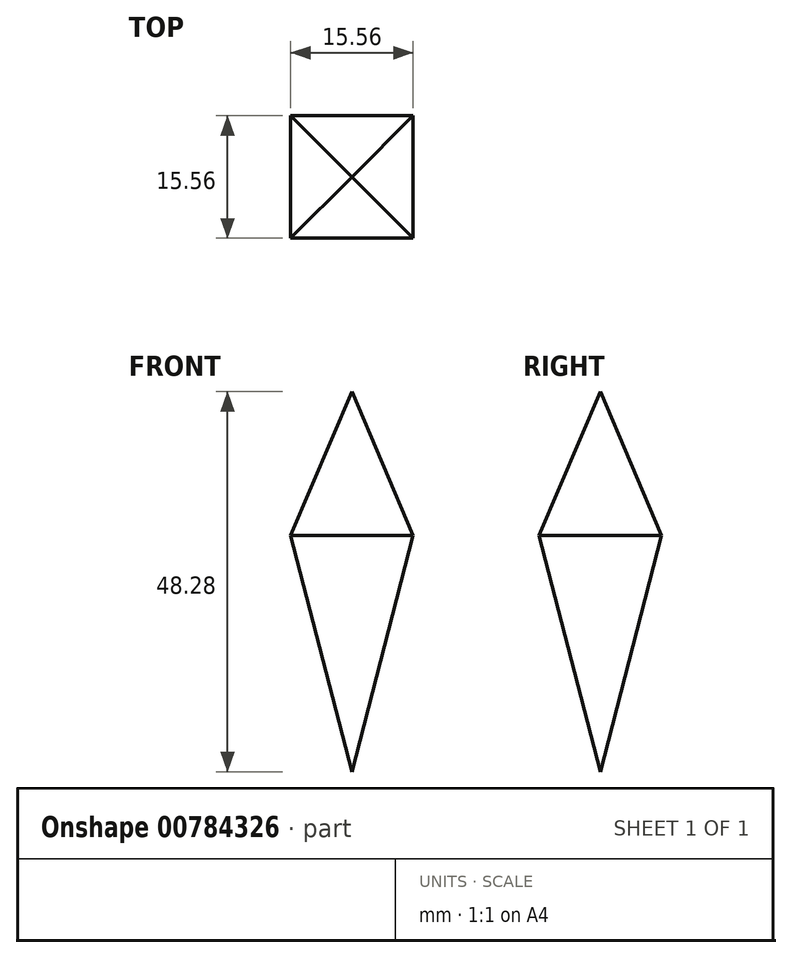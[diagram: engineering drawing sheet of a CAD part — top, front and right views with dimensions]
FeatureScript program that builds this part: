
annotation { "Feature Type Name" : "Feature", "Feature Type Description" : "" }
export const myFeature = defineFeature(function(context is Context, id is Id, definition is map)
    precondition{}
    {
        {
            var Q0;
            Q0=qCreatedBy(makeId("Front.planeOp"),FACE);
            var sketch = newSketch(context, id + "F0", { "sketchPlane" : qUnion([Q0])});
            skLineSegment(sketch, "E0", {"start": v(0, 18.23) * mm, "end": v(-7.78, 0) * mm});
            skLineSegment(sketch, "E1", {"start": v(-7.78, 0) * mm, "end": v(0, -30.05) * mm});
            skLineSegment(sketch, "E2.MirrorCS", {"start": v(0, 18.23) * mm, "end": v(7.78, 0) * mm});
            skLineSegment(sketch, "E3.MirrorCS", {"start": v(7.78, 0) * mm, "end": v(0, -30.05) * mm});
            skSolve(sketch);
        }
        {
            var Q0;
            Q0=qCreatedBy(makeId("Front.planeOp"),FACE);
            var sketch = newSketch(context, id + "F1", { "sketchPlane" : qUnion([Q0])});
            skLineSegment(sketch, "E4.0.0", {"start": v(0, -30.05) * mm, "end": v(7.78, 0) * mm});
            skLineSegment(sketch, "E4.0.1", {"start": v(7.78, 0) * mm, "end": v(0, 18.23) * mm});
            skLineSegment(sketch, "E4.0.2", {"start": v(0, 18.23) * mm, "end": v(-7.78, 0) * mm});
            skLineSegment(sketch, "E4.0.3", {"start": v(-7.78, 0) * mm, "end": v(0, -30.05) * mm});
            skSolve(sketch);
        }
        {
            var Q0;
            Q0=qCreatedBy(makeId("Front.planeOp"),FACE);
            var sketch = newSketch(context, id + "F2", { "sketchPlane" : qUnion([Q0])});
            skLineSegment(sketch, "E5", {"start": v(0, 27.69) * mm, "end": v(0, -51.93) * mm});
            skSolve(sketch);
        }
        {
            var Q0;
            Q0 = qSketchRegion(id + "F0", true);
            extrude(context, id + "F3", {"entities" : qUnion([Q0]), "endBound" : BoundingType.SYMMETRIC, "depth" : 25.4 * mm, "offsetDistance" : 25.4 * mm});
        }
        {
            var Q0;
            Q0 = qSketchRegion(id + "F1", true);
            extrude(context, id + "F4", {"entities" : qUnion([Q0]), "endBound" : BoundingType.SYMMETRIC, "depth" : 25.4 * mm, "offsetDistance" : 25.4 * mm});
        }
        {
            var Q0;
            Q0=makeQuery(id+"F3.opExtrude","SWEPT_BODY",BODY,{"disambiguationData":[OSD([sQuery(id+"F0.wireOp",EDGE,"E0"),sQuery(id+"F0.wireOp",EDGE,"E1"),sQuery(id+"F0.wireOp",EDGE,"E2.MirrorCS"),sQuery(id+"F0.wireOp",EDGE,"E3.MirrorCS")])]});
            var Q1;
            Q1=sQuery(id+"F2.wireOp",EDGE,"E5");
            transform(context, id + "F5", {"entities" : qUnion([Q0]), "transformType" : TransformType.ROTATION, "transformAxis" : qUnion([Q1]), "angle" : 90 * degree, "makeCopy" : false});
        }
        {
            var Q0;
            Q0=makeQuery(id+"F4.opExtrude","SWEPT_BODY",BODY,{"disambiguationData":[OSD([sQuery(id+"F1.wireOp",EDGE,"E4.0.0"),sQuery(id+"F1.wireOp",EDGE,"E4.0.1"),sQuery(id+"F1.wireOp",EDGE,"E4.0.2"),sQuery(id+"F1.wireOp",EDGE,"E4.0.3")])]});
            var Q1;
            Q1=makeQuery(id+"F3.opExtrude","SWEPT_BODY",BODY,{"disambiguationData":[OSD([sQuery(id+"F0.wireOp",EDGE,"E0"),sQuery(id+"F0.wireOp",EDGE,"E1"),sQuery(id+"F0.wireOp",EDGE,"E2.MirrorCS"),sQuery(id+"F0.wireOp",EDGE,"E3.MirrorCS")])]});
            booleanBodies(context, id + "F6", {"operationType" : BooleanOperationType.INTERSECTION, "tools" : qUnion([Q0, Q1])});
        }
    });
